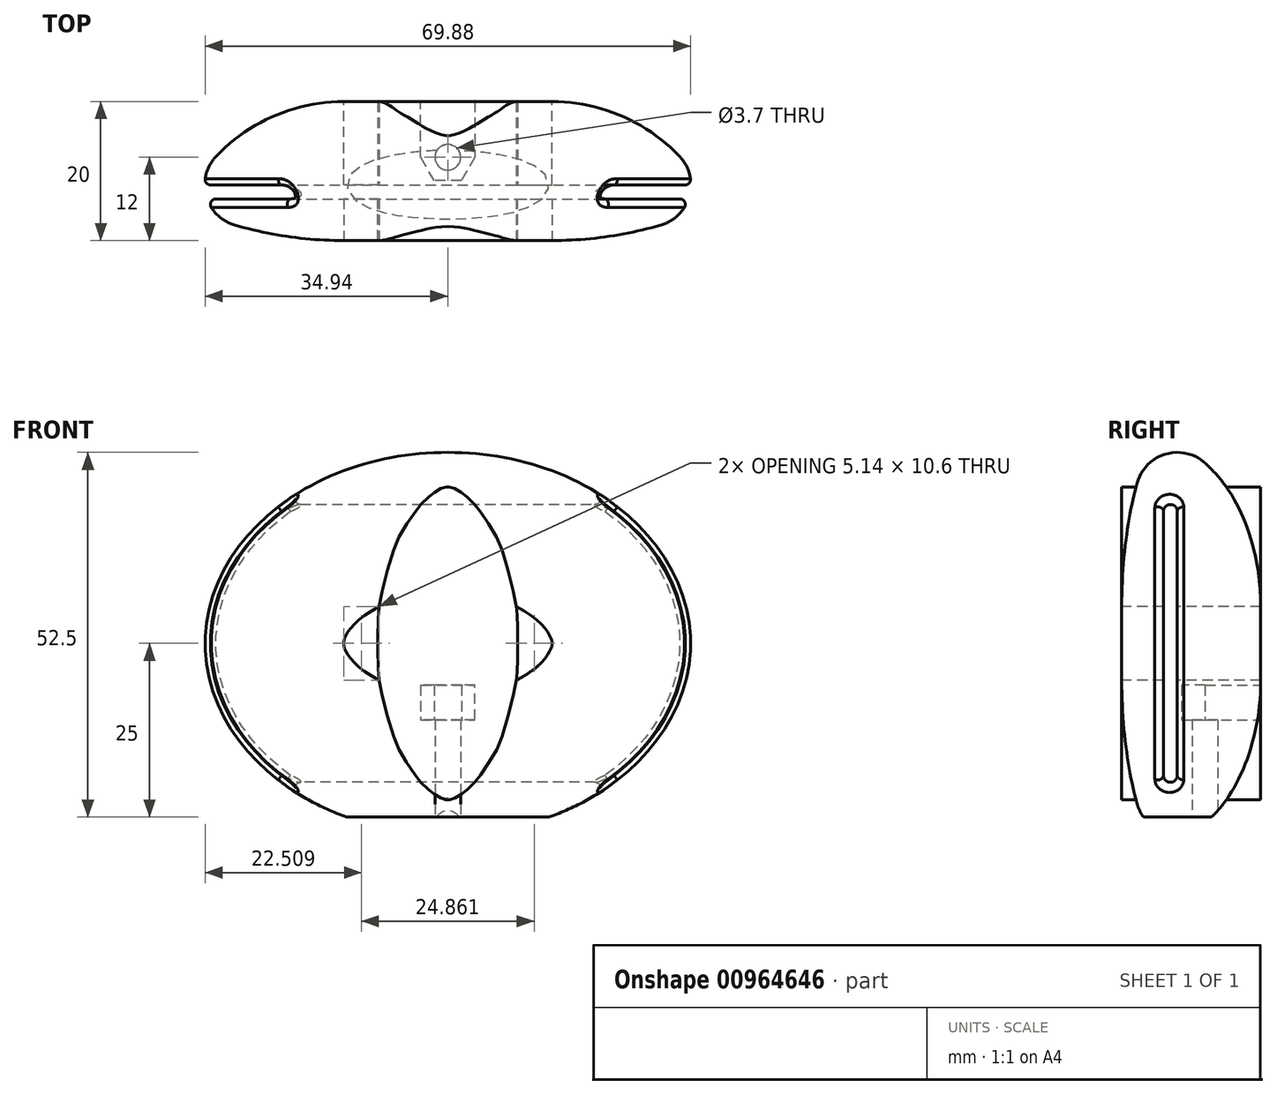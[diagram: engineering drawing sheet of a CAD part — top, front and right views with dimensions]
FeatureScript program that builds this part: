
annotation { "Feature Type Name" : "Feature", "Feature Type Description" : "" }
export const myFeature = defineFeature(function(context is Context, id is Id, definition is map)
    precondition{}
    {
        {
            var Q0;
            Q0=qCreatedBy(makeId("Front.planeOp"),FACE);
            var sketch = newSketch(context, id + "F0", { "sketchPlane" : qUnion([Q0])});
            skEllipse(sketch, "E0", {"center": v(0, 0) * mm, "majorRadius": 27.5 * mm, "minorRadius": 35 * mm, "majorAxis": v(0, 1)});
            skLineSegment(sketch, "E1", {"start": v(0, 0) * mm, "end": v(0, 27.5) * mm, "construction": true});
            skSolve(sketch);
        }
        {
            var Q0;
            Q0=qCreatedBy(makeId("Right.planeOp"),FACE);
            var sketch = newSketch(context, id + "F1", { "sketchPlane" : qUnion([Q0])});
            skCircle(sketch, "E2", {"center": v(0, 21.5) * mm, "radius": 6 * mm, "construction": true});
            skArc(sketch, "E3", {"start": v(-5.76, 23.18) * mm, "mid": v(-7.44, 15.42) * mm, "end": v(-8, 7.5) * mm});
            skArc(sketch, "E4", {"start": v(12, 7.5) * mm, "mid": v(9.95, 17.48) * mm, "end": v(4.14, 25.84) * mm});
            skLineSegment(sketch, "E5", {"start": v(-8, 7.5) * mm, "end": v(12, 7.5) * mm});
            skLineSegment(sketch, "E6", {"start": v(12, 16.14) * mm, "end": v(12, 7.5) * mm, "construction": true});
            skLineSegment(sketch, "E7", {"start": v(-8, 53.87) * mm, "end": v(-8, 7.5) * mm, "construction": true});
            skArc(sketch, "E8", {"start": v(4.14, 25.84) * mm, "mid": v(-1.56, 27.3) * mm, "end": v(-5.76, 23.18) * mm});
            skLineSegment(sketch, "E9", {"start": v(0, 21.5) * mm, "end": v(0, 7.5) * mm, "construction": true});
            skLineSegment(sketch, "E10", {"start": v(0, 21.5) * mm, "end": v(0, 27.5) * mm, "construction": true});
            skSolve(sketch);
        }
        {
            var Q0;
            Q0=makeQuery(id+"F1.imprint","IMPRINT",FACE,{"disambiguationData":[TD([[makeQuery(id+"F1.imprint","IMPRINT",EDGE,{"derivedFrom":sQuery(id+"F1.wireOp",EDGE,"E3")}),1.0]])]});
            var Q1;
            Q1=sQuery(id+"F0.wireOp",EDGE,"E0");
            sweep(context, id + "F2", {"profiles" : qUnion([Q0]), "path" : qUnion([Q1])});
        }
        {
            var Q0;
            Q0=qCreatedBy(makeId("Front.planeOp"),FACE);
            var sketch = newSketch(context, id + "F3", { "sketchPlane" : qUnion([Q0])});
            skFitSpline(sketch, "E11.0", {"points": [v(0, 22.5) * mm, v(-0.16, 22.5) * mm, v(-0.33, 22.48) * mm, v(-0.85, 22.33) * mm, v(-1.2, 22.19) * mm, v(-2.1, 21.62) * mm, v(-2.66, 21.2) * mm, v(-3.88, 19.97) * mm, v(-4.54, 19.18) * mm, v(-6.5, 16.23) * mm, v(-7.77, 13.52) * mm, v(-9.51, 7.2) * mm, v(-10, 3.6) * mm, v(-10, -3.6) * mm, v(-9.51, -7.2) * mm, v(-7.77, -13.52) * mm, v(-6.5, -16.23) * mm, v(-4.54, -19.18) * mm, v(-3.88, -19.97) * mm, v(-2.66, -21.2) * mm, v(-2.1, -21.62) * mm, v(-1.2, -22.19) * mm, v(-0.85, -22.33) * mm, v(-0.33, -22.48) * mm, v(-0.16, -22.5) * mm, v(0.16, -22.5) * mm, v(0.33, -22.48) * mm, v(0.85, -22.33) * mm, v(1.2, -22.19) * mm, v(2.1, -21.62) * mm, v(2.66, -21.2) * mm, v(3.88, -19.97) * mm, v(4.54, -19.18) * mm, v(6.5, -16.23) * mm, v(7.77, -13.52) * mm, v(9.51, -7.2) * mm, v(10, -3.6) * mm, v(10, 3.6) * mm, v(9.51, 7.2) * mm, v(7.77, 13.52) * mm, v(6.5, 16.23) * mm, v(4.54, 19.18) * mm, v(3.88, 19.97) * mm, v(2.66, 21.2) * mm, v(2.1, 21.62) * mm, v(1.2, 22.19) * mm, v(0.85, 22.33) * mm, v(0.33, 22.48) * mm, v(0.16, 22.5) * mm, v(0, 22.5) * mm]});
            skSolve(sketch);
        }
        {
            var Q0;
            Q0=qSketchRegion(id+"F3",true);
            var Q1;
            Q1=makeQuery(id+"F2.opSweep","SWEPT_FACE",FACE,{"disambiguationData":[OSD([sQuery(id+"F0.wireOp",EDGE,"E0"),sQuery(id+"F1.wireOp",EDGE,"E3")])]});
            extrude(context, id + "F4", {"entities" : qUnion([Q0]), "operationType" : NewBodyOperationType.ADD, "endBoundEntity" : qUnion([Q1]), "depth" : 8 * mm, "hasSecondDirection" : true, "secondDirectionOppositeDirection" : true, "secondDirectionDepth" : 12 * mm});
        }
        {
            var Q0;
            Q0=qCreatedBy(makeId("Right.planeOp"),FACE);
            var sketch = newSketch(context, id + "F5", { "sketchPlane" : qUnion([Q0])});
            skLineSegment(sketch, "E12.bottom", {"start": v(-2, 20) * mm, "end": v(0, 20) * mm});
            skLineSegment(sketch, "E12.top", {"start": v(-2, -20) * mm, "end": v(0, -20) * mm});
            skLineSegment(sketch, "E12.left", {"start": v(0, 20) * mm, "end": v(0, -20) * mm});
            skLineSegment(sketch, "E12.right", {"start": v(-2, 20) * mm, "end": v(-2, -20) * mm});
            skSolve(sketch);
        }
        {
            var Q0;
            Q0=qSketchRegion(id+"F5",true);
            extrude(context, id + "F6", {"entities" : qUnion([Q0]), "operationType" : NewBodyOperationType.REMOVE, "endBound" : BoundingType.THROUGH_ALL, "oppositeDirection" : true, "depth" : 25 * mm, "hasSecondDirection" : true, "secondDirectionBound" : SecondDirectionBoundingType.THROUGH_ALL, "secondDirectionOppositeDirection" : false, "secondDirectionDepth" : 25 * mm});
        }
        {
            var Q0;
            Q0=makeQuery(id+"F6.boolean.opBoolean","COPY",EDGE,{"derivedFrom":makeQuery(id+"F6.opExtrude","SWEPT_EDGE",EDGE,{"disambiguationData":[OSD([sQuery(id+"F5.wireOp",EDGE,"E12.bottom"),sQuery(id+"F5.wireOp",EDGE,"E12.right")])]})});
            var Q1;
            Q1=makeQuery(id+"F6.boolean.opBoolean","COPY",EDGE,{"derivedFrom":makeQuery(id+"F6.opExtrude","SWEPT_EDGE",EDGE,{"disambiguationData":[OSD([sQuery(id+"F5.wireOp",EDGE,"E12.bottom"),sQuery(id+"F5.wireOp",EDGE,"E12.left")])]})});
            var Q2;
            Q2=makeQuery(id+"F6.boolean.opBoolean","COPY",EDGE,{"derivedFrom":makeQuery(id+"F6.opExtrude","SWEPT_EDGE",EDGE,{"disambiguationData":[OSD([sQuery(id+"F5.wireOp",EDGE,"E12.top"),sQuery(id+"F5.wireOp",EDGE,"E12.right")])]})});
            var Q3;
            Q3=makeQuery(id+"F6.boolean.opBoolean","COPY",EDGE,{"derivedFrom":makeQuery(id+"F6.opExtrude","SWEPT_EDGE",EDGE,{"disambiguationData":[OSD([sQuery(id+"F5.wireOp",EDGE,"E12.top"),sQuery(id+"F5.wireOp",EDGE,"E12.left")])]})});
            fillet(context, id + "F7", {"entities" : qUnion([Q0, Q1, Q2, Q3]), "radius" : 1 * mm, "tangentPropagation" : true, "allowEdgeOverflow" : false});
        }
        {
            var Q0;
            Q0=qCreatedBy(makeId("Right.planeOp"),FACE);
            var sketch = newSketch(context, id + "F8", { "sketchPlane" : qUnion([Q0])});
            skLineSegment(sketch, "E13", {"start": v(-9.7, -25) * mm, "end": v(12.72, -25) * mm});
            skLineSegment(sketch, "E14", {"start": v(12.72, -25) * mm, "end": v(14.86, -55.14) * mm});
            skLineSegment(sketch, "E15", {"start": v(14.86, -55.14) * mm, "end": v(-15.13, -48.74) * mm});
            skLineSegment(sketch, "E16", {"start": v(-15.13, -48.74) * mm, "end": v(-9.7, -25) * mm});
            skLineSegment(sketch, "E17", {"start": v(0, 0) * mm, "end": v(0, -25) * mm, "construction": true});
            skSolve(sketch);
        }
        {
            var Q0;
            Q0=qSketchRegion(id+"F8",true);
            extrude(context, id + "F9", {"entities" : qUnion([Q0]), "operationType" : NewBodyOperationType.REMOVE, "endBound" : BoundingType.THROUGH_ALL, "oppositeDirection" : true, "depth" : 25 * mm, "hasSecondDirection" : true, "secondDirectionBound" : SecondDirectionBoundingType.THROUGH_ALL, "secondDirectionOppositeDirection" : false, "secondDirectionDepth" : 25 * mm});
        }
        {
            var Q0;
            Q0=makeQuery(id+"F9.boolean.opBoolean","COPY",FACE,{"derivedFrom":makeQuery(id+"F9.opExtrude","SWEPT_FACE",FACE,{"disambiguationData":[OSD([sQuery(id+"F8.wireOp",EDGE,"E13")])]})});
            var sketch = newSketch(context, id + "F10", { "sketchPlane" : qUnion([Q0])});
            skCircle(sketch, "E18", {"center": v(0, -4) * mm, "radius": 1.85 * mm});
            skLineSegment(sketch, "E19", {"start": v(0, 0) * mm, "end": v(0, -4) * mm, "construction": true});
            skSolve(sketch);
        }
        {
            var Q0;
            Q0=qSketchRegion(id+"F10",true);
            extrude(context, id + "F11", {"entities" : qUnion([Q0]), "operationType" : NewBodyOperationType.REMOVE, "oppositeDirection" : true, "depth" : 14 * mm});
        }
        {
            var Q0;
            Q0=makeQuery(id+"F6.boolean.opBoolean","INTERSECT",EDGE,{"disambiguationData":[OD(1.0)],"derivedFrom":[makeQuery(id+"F2.opSweep","SWEPT_FACE",FACE,{"disambiguationData":[OSD([sQuery(id+"F0.wireOp",EDGE,"E0"),sQuery(id+"F1.wireOp",EDGE,"E8")])]}),makeQuery(id+"F6.opExtrude","SWEPT_FACE",FACE,{"disambiguationData":[OSD([sQuery(id+"F5.wireOp",EDGE,"E12.left")])]})]});
            var Q1;
            Q1=makeQuery(id+"F6.boolean.opBoolean","INTERSECT",EDGE,{"disambiguationData":[OD(0.0)],"derivedFrom":[makeQuery(id+"F2.opSweep","SWEPT_FACE",FACE,{"disambiguationData":[OSD([sQuery(id+"F0.wireOp",EDGE,"E0"),sQuery(id+"F1.wireOp",EDGE,"E8")])]}),makeQuery(id+"F6.opExtrude","SWEPT_FACE",FACE,{"disambiguationData":[OSD([sQuery(id+"F5.wireOp",EDGE,"E12.left")])]})]});
            fillet(context, id + "F12", {"entities" : qUnion([Q0, Q1]), "radius" : .8 * mm, "tangentPropagation" : true, "allowEdgeOverflow" : false});
        }
        {
            var Q0;
            Q0=makeQuery(id+"F11.boolean.opBoolean","COPY",FACE,{"derivedFrom":makeQuery(id+"F11.opExtrude","CAP_FACE",FACE,{"disambiguationData":[OSD([sQuery(id+"F10.wireOp",EDGE,"E18")])],"isStart":false})});
            var sketch = newSketch(context, id + "F13", { "sketchPlane" : qUnion([Q0])});
            skLineSegment(sketch, "E20", {"start": v(1.95, -0.62) * mm, "end": v(-1.95, -0.62) * mm});
            skLineSegment(sketch, "E21", {"start": v(-1.95, -0.62) * mm, "end": v(-3.9, -4) * mm});
            skLineSegment(sketch, "E22", {"start": v(-3.9, -4) * mm, "end": v(-3.9, -13.51) * mm});
            skLineSegment(sketch, "E23", {"start": v(-3.9, -13.51) * mm, "end": v(3.9, -13.51) * mm});
            skLineSegment(sketch, "E24", {"start": v(3.9, -13.51) * mm, "end": v(3.9, -4) * mm});
            skLineSegment(sketch, "E25", {"start": v(3.9, -4) * mm, "end": v(1.95, -0.62) * mm});
            skCircle(sketch, "E26", {"center": v(0, -4) * mm, "radius": 3.9 * mm, "construction": true});
            skSolve(sketch);
        }
        {
            var Q0;
            Q0=qSketchRegion(id+"F13",true);
            extrude(context, id + "F14", {"entities" : qUnion([Q0]), "operationType" : NewBodyOperationType.REMOVE, "oppositeDirection" : true, "depth" : 5 * mm});
        }
    });
